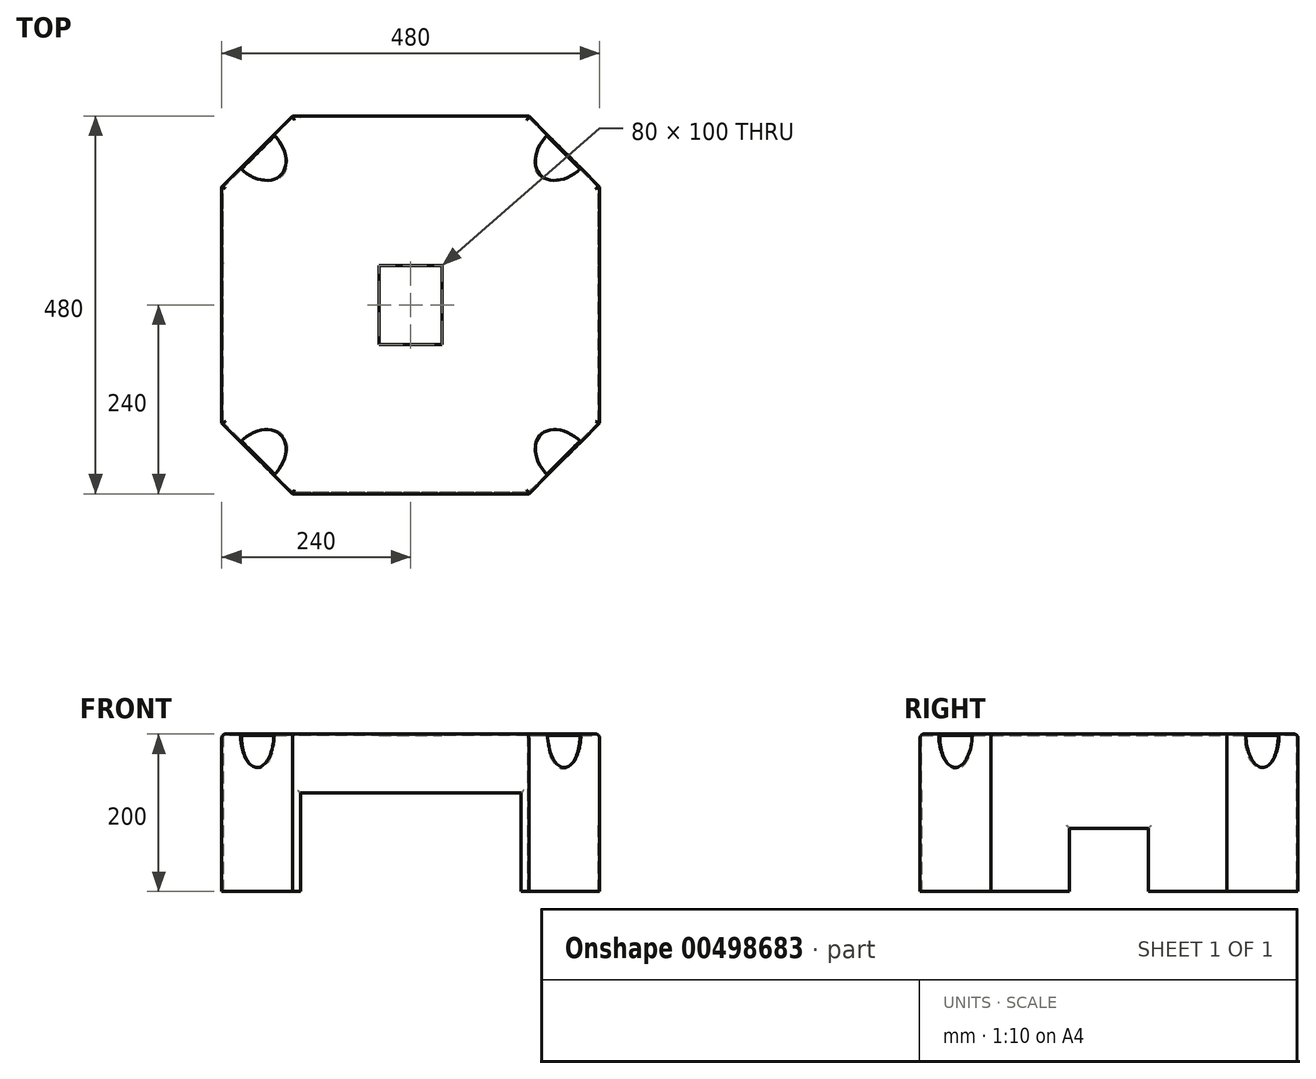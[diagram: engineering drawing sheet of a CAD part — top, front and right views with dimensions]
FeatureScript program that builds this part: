
annotation { "Feature Type Name" : "Feature", "Feature Type Description" : "" }
export const myFeature = defineFeature(function(context is Context, id is Id, definition is map)
    precondition{}
    {
        {
            var Q0;
            Q0=qCreatedBy(makeId("Front.planeOp"),FACE);
            var sketch = newSketch(context, id + "F0", { "sketchPlane" : qUnion([Q0])});
            skLineSegment(sketch, "E0.bottom", {"start": v(240, -100) * mm, "end": v(-240, -100) * mm});
            skLineSegment(sketch, "E0.top", {"start": v(240, 100) * mm, "end": v(-240, 100) * mm});
            skLineSegment(sketch, "E0.left", {"start": v(240, -100) * mm, "end": v(240, 100) * mm});
            skLineSegment(sketch, "E0.right", {"start": v(-240, -100) * mm, "end": v(-240, 100) * mm});
            skPoint(sketch, "E0.middle", {"position": v(0, 0) * mm});
            skLineSegment(sketch, "E1", {"start": v(0, 0) * mm, "end": v(0, -124.49) * mm, "construction": true});
            skPoint(sketch, "E1.endSnap0", {"position": v(0, -100) * mm});
            skLineSegment(sketch, "E2", {"start": v(0, -100) * mm, "end": v(140, -100) * mm});
            skLineSegment(sketch, "E3", {"start": v(140, -100) * mm, "end": v(140, 25) * mm});
            skLineSegment(sketch, "E4", {"start": v(140, 25) * mm, "end": v(-140, 25) * mm});
            skLineSegment(sketch, "E5", {"start": v(-140, 25) * mm, "end": v(-140, -100) * mm});
            skLineSegment(sketch, "E6", {"start": v(-140, -100) * mm, "end": v(0, -100) * mm});
            skSolve(sketch);
        }
        {
            var Q0;
            Q0=makeQuery(id+"F0.imprint","IMPRINT",FACE,{"disambiguationData":[TD([[makeQuery(id+"F0.imprint","IMPRINT",EDGE,{"derivedFrom":sQuery(id+"F0.wireOp",EDGE,"E0.top")}),1.0]])]});
            extrude(context, id + "F1", {"entities" : qUnion([Q0]), "endBound" : BoundingType.SYMMETRIC, "depth" : 480 * mm});
        }
        {
            var Q0;
            Q0=makeQuery(id+"F1.opExtrude","CAP_EDGE",EDGE,{"disambiguationData":[OSD([sQuery(id+"F0.wireOp",EDGE,"E0.left")])],"isStart":false});
            var Q1;
            Q1=makeQuery(id+"F1.opExtrude","CAP_EDGE",EDGE,{"disambiguationData":[OSD([sQuery(id+"F0.wireOp",EDGE,"E0.left")])],"isStart":true});
            var Q2;
            Q2=makeQuery(id+"F1.opExtrude","CAP_EDGE",EDGE,{"disambiguationData":[OSD([sQuery(id+"F0.wireOp",EDGE,"E0.right")])],"isStart":true});
            var Q3;
            Q3=makeQuery(id+"F1.opExtrude","CAP_EDGE",EDGE,{"disambiguationData":[OSD([sQuery(id+"F0.wireOp",EDGE,"E0.right")])],"isStart":false});
            chamfer(context, id + "F2", {"entities" : qUnion([Q0, Q1, Q2, Q3]), "width" : 90 * mm, "tangentPropagation" : true});
        }
        {
            var Q0;
            {var subQ0=sQuery(id+"F0.wireOp",EDGE,"E0.bottom");Q0=makeQuery(id+"F1.opExtrude","SWEPT_FACE",FACE,{"disambiguationData":[OSD([subQ0]),TDD([makeQuery(id+"F0.imprint","IMPRINT",EDGE,{"disambiguationData":[TD([[makeQuery(id+"F0.imprint","INTERSECT",VERTEX,{"derivedFrom":[subQ0,sQuery(id+"F0.wireOp",EDGE,"E0.left")]}),-1.0]])],"derivedFrom":subQ0})])]});}
            var Q1;
            {var subQ0=sQuery(id+"F0.wireOp",EDGE,"E0.bottom");Q1=makeQuery(id+"F1.opExtrude","SWEPT_FACE",FACE,{"disambiguationData":[OSD([subQ0]),TDD([makeQuery(id+"F0.imprint","IMPRINT",EDGE,{"disambiguationData":[TD([[makeQuery(id+"F0.imprint","INTERSECT",VERTEX,{"derivedFrom":[subQ0,sQuery(id+"F0.wireOp",EDGE,"E0.right")]}),1.0]])],"derivedFrom":subQ0})])]});}
            var Q2;
            Q2=makeQuery(id+"F1.opExtrude","SWEPT_FACE",FACE,{"disambiguationData":[OSD([sQuery(id+"F0.wireOp",EDGE,"E4")])]});
            var Q3;
            Q3=makeQuery(id+"F1.opExtrude","SWEPT_FACE",FACE,{"disambiguationData":[OSD([sQuery(id+"F0.wireOp",EDGE,"E3")])]});
            var Q4;
            Q4=makeQuery(id+"F1.opExtrude","SWEPT_FACE",FACE,{"disambiguationData":[OSD([sQuery(id+"F0.wireOp",EDGE,"E5")])]});
            shell(context, id + "F3", {"entities" : qUnion([Q0, Q1, Q2, Q3, Q4]), "thickness" : 1.6 * mm});
        }
        {
            var Q0;
            Q0=makeQuery(id+"F2.opChamfer","BLEND_EDGE",EDGE,{"blendedFrom":[makeQuery(id+"F1.opExtrude","CAP_EDGE",EDGE,{"disambiguationData":[OSD([sQuery(id+"F0.wireOp",EDGE,"E0.right")])],"isStart":true}),makeQuery(id+"F1.opExtrude","SWEPT_FACE",FACE,{"disambiguationData":[OSD([sQuery(id+"F0.wireOp",EDGE,"E0.top")])]})],"blendedInto":[makeQuery(id+"F1.opExtrude","SWEPT_FACE",FACE,{"disambiguationData":[OSD([sQuery(id+"F0.wireOp",EDGE,"E0.top")])]})]});
            cPlane(context, id + "F4", {"entities" : qUnion([Q0]), "cplaneType" : CPlaneType.LINE_ANGLE, "offset" : 25 * mm, "angle" : 45 * degree, "width" : 150 * mm, "height" : 150 * mm});
        }
        {
            var Q0;
            Q0=makeQuery(id+"F2.opChamfer","BLEND_EDGE",EDGE,{"blendedFrom":[makeQuery(id+"F1.opExtrude","CAP_EDGE",EDGE,{"disambiguationData":[OSD([sQuery(id+"F0.wireOp",EDGE,"E0.right")])],"isStart":false}),makeQuery(id+"F1.opExtrude","SWEPT_FACE",FACE,{"disambiguationData":[OSD([sQuery(id+"F0.wireOp",EDGE,"E0.top")])]})],"blendedInto":[makeQuery(id+"F1.opExtrude","SWEPT_FACE",FACE,{"disambiguationData":[OSD([sQuery(id+"F0.wireOp",EDGE,"E0.top")])]})]});
            cPlane(context, id + "F5", {"entities" : qUnion([Q0]), "cplaneType" : CPlaneType.LINE_ANGLE, "offset" : 25 * mm, "angle" : 45 * degree, "oppositeDirection" : true, "width" : 150 * mm, "height" : 150 * mm});
        }
        {
            var Q0;
            Q0=makeQuery(id+"F2.opChamfer","BLEND_EDGE",EDGE,{"blendedFrom":[makeQuery(id+"F1.opExtrude","CAP_EDGE",EDGE,{"disambiguationData":[OSD([sQuery(id+"F0.wireOp",EDGE,"E0.left")])],"isStart":false}),makeQuery(id+"F1.opExtrude","SWEPT_FACE",FACE,{"disambiguationData":[OSD([sQuery(id+"F0.wireOp",EDGE,"E0.top")])]})],"blendedInto":[makeQuery(id+"F1.opExtrude","SWEPT_FACE",FACE,{"disambiguationData":[OSD([sQuery(id+"F0.wireOp",EDGE,"E0.top")])]})]});
            cPlane(context, id + "F6", {"entities" : qUnion([Q0]), "cplaneType" : CPlaneType.LINE_ANGLE, "offset" : 25 * mm, "angle" : 45 * degree, "width" : 150 * mm, "height" : 150 * mm});
        }
        {
            var Q0;
            Q0=makeQuery(id+"F2.opChamfer","BLEND_EDGE",EDGE,{"blendedFrom":[makeQuery(id+"F1.opExtrude","CAP_EDGE",EDGE,{"disambiguationData":[OSD([sQuery(id+"F0.wireOp",EDGE,"E0.left")])],"isStart":true}),makeQuery(id+"F1.opExtrude","SWEPT_FACE",FACE,{"disambiguationData":[OSD([sQuery(id+"F0.wireOp",EDGE,"E0.top")])]})],"blendedInto":[makeQuery(id+"F1.opExtrude","SWEPT_FACE",FACE,{"disambiguationData":[OSD([sQuery(id+"F0.wireOp",EDGE,"E0.top")])]})]});
            cPlane(context, id + "F7", {"entities" : qUnion([Q0]), "cplaneType" : CPlaneType.LINE_ANGLE, "offset" : 25 * mm, "angle" : 45 * degree, "oppositeDirection" : true, "width" : 150 * mm, "height" : 150 * mm});
        }
        {
            var Q0;
            Q0=qCreatedBy(id+"F6.planeOp",FACE);
            var sketch = newSketch(context, id + "F8", { "sketchPlane" : qUnion([Q0])});
            skCircle(sketch, "E7", {"center": v(71.76, -101.48) * mm, "radius": 30 * mm});
            skPoint(sketch, "E8.trimOffspring.end.orphan", {"position": v(123.72, -64.74) * mm});
            skPoint(sketch, "E9.0.start.orphan", {"position": v(19.8, -138.22) * mm});
            skSolve(sketch);
        }
        {
            var Q0;
            Q0=qCreatedBy(id+"F7.planeOp",FACE);
            var sketch = newSketch(context, id + "F9", { "sketchPlane" : qUnion([Q0])});
            skCircle(sketch, "E10", {"center": v(71.76, -101.48) * mm, "radius": 30 * mm});
            skPoint(sketch, "E11.trimOffspring.end.orphan", {"position": v(19.8, -138.22) * mm});
            skPoint(sketch, "E12.0.start.orphan", {"position": v(123.72, -64.74) * mm});
            skSolve(sketch);
        }
        {
            var Q0;
            Q0=qCreatedBy(id+"F4.planeOp",FACE);
            var sketch = newSketch(context, id + "F10", { "sketchPlane" : qUnion([Q0])});
            skCircle(sketch, "E13", {"center": v(-71.76, -101.48) * mm, "radius": 30 * mm});
            skPoint(sketch, "E14.orphan", {"position": v(-19.8, -138.22) * mm});
            skPoint(sketch, "E15.0.end.orphan", {"position": v(-123.72, -64.74) * mm});
            skSolve(sketch);
        }
        {
            var Q0;
            Q0=qCreatedBy(id+"F5.planeOp",FACE);
            var sketch = newSketch(context, id + "F11", { "sketchPlane" : qUnion([Q0])});
            skCircle(sketch, "E16", {"center": v(-71.76, -101.48) * mm, "radius": 30 * mm});
            skPoint(sketch, "E17.orphan", {"position": v(-123.72, -64.74) * mm});
            skPoint(sketch, "E18.0.end.orphan", {"position": v(-19.8, -138.22) * mm});
            skSolve(sketch);
        }
        {
            var Q0;
            Q0=makeQuery(id+"F10.imprint","IMPRINT",FACE,{"disambiguationData":[TD([[makeQuery(id+"F10.imprint","IMPRINT",EDGE,{"derivedFrom":sQuery(id+"F10.wireOp",EDGE,"E13")}),1.0]])]});
            extrude(context, id + "F12", {"entities" : qUnion([Q0]), "operationType" : NewBodyOperationType.REMOVE, "depth" : 78 * mm});
        }
        {
            var Q0;
            Q0=makeQuery(id+"F11.imprint","IMPRINT",FACE,{"disambiguationData":[TD([[makeQuery(id+"F11.imprint","IMPRINT",EDGE,{"derivedFrom":sQuery(id+"F11.wireOp",EDGE,"E16")}),1.0]])]});
            extrude(context, id + "F13", {"entities" : qUnion([Q0]), "operationType" : NewBodyOperationType.REMOVE, "oppositeDirection" : true, "depth" : 82 * mm});
        }
        {
            var Q0;
            Q0=makeQuery(id+"F8.imprint","IMPRINT",FACE,{"disambiguationData":[TD([[makeQuery(id+"F8.imprint","IMPRINT",EDGE,{"derivedFrom":sQuery(id+"F8.wireOp",EDGE,"E7")}),1.0]])]});
            extrude(context, id + "F14", {"entities" : qUnion([Q0]), "operationType" : NewBodyOperationType.REMOVE, "oppositeDirection" : true, "depth" : 153 * mm});
        }
        {
            var Q0;
            Q0=makeQuery(id+"F9.imprint","IMPRINT",FACE,{"disambiguationData":[TD([[makeQuery(id+"F9.imprint","IMPRINT",EDGE,{"derivedFrom":sQuery(id+"F9.wireOp",EDGE,"E10")}),1.0]])]});
            extrude(context, id + "F15", {"entities" : qUnion([Q0]), "operationType" : NewBodyOperationType.REMOVE, "depth" : 141 * mm});
        }
        {
            var Q0;
            Q0=makeQuery(id+"F1.opExtrude","SWEPT_FACE",FACE,{"disambiguationData":[OSD([sQuery(id+"F0.wireOp",EDGE,"E0.right")])]});
            var sketch = newSketch(context, id + "F16", { "sketchPlane" : qUnion([Q0])});
            skLineSegment(sketch, "E19.0.0", {"start": v(-50, -100) * mm, "end": v(50, -100) * mm});
            skPoint(sketch, "E20.endSnap0", {"position": v(0, -100) * mm});
            skLineSegment(sketch, "E21", {"start": v(0, -100) * mm, "end": v(-50, -100) * mm});
            skLineSegment(sketch, "E22", {"start": v(-50, -100) * mm, "end": v(-50, -20) * mm});
            skLineSegment(sketch, "E23", {"start": v(-50, -20) * mm, "end": v(50, -20) * mm});
            skLineSegment(sketch, "E24", {"start": v(50, -20) * mm, "end": v(50, -100) * mm});
            skLineSegment(sketch, "E25", {"start": v(50, -100) * mm, "end": v(0, -100) * mm});
            skPoint(sketch, "E19.0.1.start.orphan", {"position": v(150, -100) * mm});
            skPoint(sketch, "E19.0.2.start.orphan", {"position": v(150, 100) * mm});
            skPoint(sketch, "E19.0.3.end.orphan", {"position": v(-150, -100) * mm});
            skPoint(sketch, "E19.0.3.start.orphan", {"position": v(-150, 100) * mm});
            skPoint(sketch, "E20.end.orphan", {"position": v(0, -20) * mm});
            skSolve(sketch);
        }
        {
            var Q0;
            Q0 = qSketchRegion(id + "F16", true);
            extrude(context, id + "F17", {"entities" : qUnion([Q0]), "operationType" : NewBodyOperationType.REMOVE, "oppositeDirection" : true, "depth" : 688 * mm});
        }
        {
            var Q0;
            Q0=makeQuery(id+"F1.opExtrude","SWEPT_FACE",FACE,{"disambiguationData":[OSD([sQuery(id+"F0.wireOp",EDGE,"E0.top")])]});
            var sketch = newSketch(context, id + "F18", { "sketchPlane" : qUnion([Q0])});
            skLineSegment(sketch, "E26.bottom", {"start": v(40, -50) * mm, "end": v(-40, -50) * mm});
            skLineSegment(sketch, "E26.top", {"start": v(40, 50) * mm, "end": v(-40, 50) * mm});
            skLineSegment(sketch, "E26.left", {"start": v(40, -50) * mm, "end": v(40, 50) * mm});
            skLineSegment(sketch, "E26.right", {"start": v(-40, -50) * mm, "end": v(-40, 50) * mm});
            skPoint(sketch, "E26.middle", {"position": v(0, 0) * mm});
            skPoint(sketch, "E27.0.3.start.orphan", {"position": v(-150, 240) * mm});
            skPoint(sketch, "E27.0.4.end.orphan", {"position": v(-173.79, 216.21) * mm});
            skPoint(sketch, "E27.0.5.start.orphan", {"position": v(-216.21, 173.79) * mm});
            skPoint(sketch, "E27.0.6.start.orphan", {"position": v(-240, 150) * mm});
            skPoint(sketch, "E27.0.7.start.orphan", {"position": v(-240, -150) * mm});
            skPoint(sketch, "E27.0.8.end.orphan", {"position": v(-216.21, -173.79) * mm});
            skPoint(sketch, "E27.0.9.start.orphan", {"position": v(-173.79, -216.21) * mm});
            skPoint(sketch, "E27.0.10.start.orphan", {"position": v(-150, -240) * mm});
            skPoint(sketch, "E27.0.11.start.orphan", {"position": v(150, -240) * mm});
            skPoint(sketch, "E27.0.12.end.orphan", {"position": v(173.79, -216.21) * mm});
            skPoint(sketch, "E27.0.13.start.orphan", {"position": v(216.21, -173.79) * mm});
            skPoint(sketch, "E27.0.14.start.orphan", {"position": v(240, -150) * mm});
            skPoint(sketch, "E27.0.15.start.orphan", {"position": v(240, 150) * mm});
            skPoint(sketch, "E27.0.1.end.orphan", {"position": v(150, 240) * mm});
            skPoint(sketch, "E27.0.0.end.orphan", {"position": v(216.21, 173.79) * mm});
            skPoint(sketch, "E27.0.0.start.orphan", {"position": v(173.79, 216.21) * mm});
            skLineSegment(sketch, "E28", {"start": v(0, -50) * mm, "end": v(0, 59.6) * mm, "construction": true});
            skSolve(sketch);
        }
        {
            var Q0;
            Q0 = qSketchRegion(id + "F18", true);
            extrude(context, id + "F19", {"entities" : qUnion([Q0]), "operationType" : NewBodyOperationType.REMOVE, "oppositeDirection" : true, "depth" : 25 * mm});
        }
        {
            var Q0;
            Q0=makeQuery(id+"F1.opExtrude","CAP_EDGE",EDGE,{"disambiguationData":[OSD([sQuery(id+"F0.wireOp",EDGE,"E0.top")])],"isStart":true});
            var Q1;
            {var subQ0=sQuery(id+"F0.wireOp",EDGE,"E0.right");var subQ1=sQuery(id+"F0.wireOp",EDGE,"E0.top");var subQ2=makeQuery(id+"F1.opExtrude","SWEPT_FACE",FACE,{"disambiguationData":[OSD([subQ1])]});var subQ3=makeQuery(id+"F1.opExtrude","CAP_EDGE",EDGE,{"disambiguationData":[OSD([subQ0])],"isStart":true});Q1=makeQuery(id+"F12.boolean.opBoolean","SPLIT",EDGE,{"disambiguationData":[TD([makeQuery(id+"F1.opExtrude","CAP_FACE",FACE,{"disambiguationData":[OSD([sQuery(id+"F0.wireOp",EDGE,"E0.bottom"),subQ1,sQuery(id+"F0.wireOp",EDGE,"E0.left"),subQ0,sQuery(id+"F0.wireOp",EDGE,"E3"),sQuery(id+"F0.wireOp",EDGE,"E4"),sQuery(id+"F0.wireOp",EDGE,"E5")])],"isStart":true})])],"derivedFrom":makeQuery(id+"F2.opChamfer","BLEND_EDGE",EDGE,{"blendedFrom":[subQ3,subQ2],"blendedInto":[subQ2]})});}
            var Q2;
            {var subQ0=sQuery(id+"F0.wireOp",EDGE,"E0.left");var subQ1=sQuery(id+"F0.wireOp",EDGE,"E0.top");var subQ2=makeQuery(id+"F1.opExtrude","CAP_EDGE",EDGE,{"disambiguationData":[OSD([subQ0])],"isStart":true});var subQ3=makeQuery(id+"F1.opExtrude","SWEPT_FACE",FACE,{"disambiguationData":[OSD([subQ1])]});Q2=makeQuery(id+"F15.boolean.opBoolean","SPLIT",EDGE,{"disambiguationData":[TD([makeQuery(id+"F1.opExtrude","CAP_FACE",FACE,{"disambiguationData":[OSD([sQuery(id+"F0.wireOp",EDGE,"E0.bottom"),subQ1,subQ0,sQuery(id+"F0.wireOp",EDGE,"E0.right"),sQuery(id+"F0.wireOp",EDGE,"E3"),sQuery(id+"F0.wireOp",EDGE,"E4"),sQuery(id+"F0.wireOp",EDGE,"E5")])],"isStart":true})])],"derivedFrom":makeQuery(id+"F2.opChamfer","BLEND_EDGE",EDGE,{"blendedFrom":[subQ2,subQ3],"blendedInto":[subQ3]})});}
            var Q3;
            {var subQ0=makeQuery(id+"F1.opExtrude","SWEPT_FACE",FACE,{"disambiguationData":[OSD([sQuery(id+"F0.wireOp",EDGE,"E0.top")])]});var subQ1=sQuery(id+"F0.wireOp",EDGE,"E0.left");var subQ2=makeQuery(id+"F1.opExtrude","CAP_EDGE",EDGE,{"disambiguationData":[OSD([subQ1])],"isStart":true});Q3=makeQuery(id+"F15.boolean.opBoolean","SPLIT",EDGE,{"disambiguationData":[TD([makeQuery(id+"F1.opExtrude","SWEPT_FACE",FACE,{"disambiguationData":[OSD([subQ1])]})])],"derivedFrom":makeQuery(id+"F2.opChamfer","BLEND_EDGE",EDGE,{"blendedFrom":[subQ2,subQ0],"blendedInto":[subQ0]})});}
            var Q4;
            {var subQ0=makeQuery(id+"F1.opExtrude","SWEPT_FACE",FACE,{"disambiguationData":[OSD([sQuery(id+"F0.wireOp",EDGE,"E0.top")])]});var subQ1=sQuery(id+"F0.wireOp",EDGE,"E0.right");var subQ2=makeQuery(id+"F1.opExtrude","CAP_EDGE",EDGE,{"disambiguationData":[OSD([subQ1])],"isStart":true});Q4=makeQuery(id+"F12.boolean.opBoolean","SPLIT",EDGE,{"disambiguationData":[TD([makeQuery(id+"F1.opExtrude","SWEPT_FACE",FACE,{"disambiguationData":[OSD([subQ1])]})])],"derivedFrom":makeQuery(id+"F2.opChamfer","BLEND_EDGE",EDGE,{"blendedFrom":[subQ2,subQ0],"blendedInto":[subQ0]})});}
            var Q5;
            Q5=makeQuery(id+"F1.opExtrude","SWEPT_EDGE",EDGE,{"disambiguationData":[OSD([sQuery(id+"F0.wireOp",EDGE,"E0.top"),sQuery(id+"F0.wireOp",EDGE,"E0.right")])]});
            var Q6;
            {var subQ0=makeQuery(id+"F1.opExtrude","SWEPT_FACE",FACE,{"disambiguationData":[OSD([sQuery(id+"F0.wireOp",EDGE,"E0.top")])]});var subQ1=sQuery(id+"F0.wireOp",EDGE,"E0.right");var subQ2=makeQuery(id+"F1.opExtrude","CAP_EDGE",EDGE,{"disambiguationData":[OSD([subQ1])],"isStart":false});Q6=makeQuery(id+"F13.boolean.opBoolean","SPLIT",EDGE,{"disambiguationData":[TD([makeQuery(id+"F1.opExtrude","SWEPT_FACE",FACE,{"disambiguationData":[OSD([subQ1])]})])],"derivedFrom":makeQuery(id+"F2.opChamfer","BLEND_EDGE",EDGE,{"blendedFrom":[subQ2,subQ0],"blendedInto":[subQ0]})});}
            var Q7;
            {var subQ0=sQuery(id+"F0.wireOp",EDGE,"E0.right");var subQ1=sQuery(id+"F0.wireOp",EDGE,"E0.top");var subQ2=makeQuery(id+"F1.opExtrude","SWEPT_FACE",FACE,{"disambiguationData":[OSD([subQ1])]});var subQ3=makeQuery(id+"F1.opExtrude","CAP_EDGE",EDGE,{"disambiguationData":[OSD([subQ0])],"isStart":false});Q7=makeQuery(id+"F13.boolean.opBoolean","SPLIT",EDGE,{"disambiguationData":[TD([makeQuery(id+"F1.opExtrude","CAP_FACE",FACE,{"disambiguationData":[OSD([sQuery(id+"F0.wireOp",EDGE,"E0.bottom"),subQ1,sQuery(id+"F0.wireOp",EDGE,"E0.left"),subQ0,sQuery(id+"F0.wireOp",EDGE,"E3"),sQuery(id+"F0.wireOp",EDGE,"E4"),sQuery(id+"F0.wireOp",EDGE,"E5")])],"isStart":false})])],"derivedFrom":makeQuery(id+"F2.opChamfer","BLEND_EDGE",EDGE,{"blendedFrom":[subQ3,subQ2],"blendedInto":[subQ2]})});}
            var Q8;
            Q8=makeQuery(id+"F1.opExtrude","CAP_EDGE",EDGE,{"disambiguationData":[OSD([sQuery(id+"F0.wireOp",EDGE,"E0.top")])],"isStart":false});
            var Q9;
            {var subQ0=makeQuery(id+"F1.opExtrude","SWEPT_FACE",FACE,{"disambiguationData":[OSD([sQuery(id+"F0.wireOp",EDGE,"E0.top")])]});var subQ1=sQuery(id+"F0.wireOp",EDGE,"E0.left");var subQ2=makeQuery(id+"F1.opExtrude","CAP_EDGE",EDGE,{"disambiguationData":[OSD([subQ1])],"isStart":false});Q9=makeQuery(id+"F14.boolean.opBoolean","SPLIT",EDGE,{"disambiguationData":[TD([makeQuery(id+"F1.opExtrude","SWEPT_FACE",FACE,{"disambiguationData":[OSD([subQ1])]})])],"derivedFrom":makeQuery(id+"F2.opChamfer","BLEND_EDGE",EDGE,{"blendedFrom":[subQ2,subQ0],"blendedInto":[subQ0]})});}
            var Q10;
            {var subQ0=sQuery(id+"F0.wireOp",EDGE,"E0.left");var subQ1=sQuery(id+"F0.wireOp",EDGE,"E0.top");var subQ2=makeQuery(id+"F1.opExtrude","CAP_EDGE",EDGE,{"disambiguationData":[OSD([subQ0])],"isStart":false});var subQ3=makeQuery(id+"F1.opExtrude","SWEPT_FACE",FACE,{"disambiguationData":[OSD([subQ1])]});Q10=makeQuery(id+"F14.boolean.opBoolean","SPLIT",EDGE,{"disambiguationData":[TD([makeQuery(id+"F1.opExtrude","CAP_FACE",FACE,{"disambiguationData":[OSD([sQuery(id+"F0.wireOp",EDGE,"E0.bottom"),subQ1,subQ0,sQuery(id+"F0.wireOp",EDGE,"E0.right"),sQuery(id+"F0.wireOp",EDGE,"E3"),sQuery(id+"F0.wireOp",EDGE,"E4"),sQuery(id+"F0.wireOp",EDGE,"E5")])],"isStart":false})])],"derivedFrom":makeQuery(id+"F2.opChamfer","BLEND_EDGE",EDGE,{"blendedFrom":[subQ2,subQ3],"blendedInto":[subQ3]})});}
            var Q11;
            Q11=makeQuery(id+"F1.opExtrude","SWEPT_EDGE",EDGE,{"disambiguationData":[OSD([sQuery(id+"F0.wireOp",EDGE,"E0.top"),sQuery(id+"F0.wireOp",EDGE,"E0.left")])]});
            var Q12;
            {var subQ0=sQuery(id+"F0.wireOp",EDGE,"E3");Q12=makeQuery(id+"F3.opShell","OFFSET_EDGE",EDGE,{"disambiguationData":[OSD([subQ0]),TDD([makeQuery(id+"F1.opExtrude","CAP_EDGE",EDGE,{"disambiguationData":[OSD([subQ0])],"isStart":false})])]});}
            var Q13;
            {var subQ0=sQuery(id+"F0.wireOp",EDGE,"E4");Q13=makeQuery(id+"F3.opShell","OFFSET_EDGE",EDGE,{"disambiguationData":[OSD([subQ0]),TDD([makeQuery(id+"F1.opExtrude","CAP_EDGE",EDGE,{"disambiguationData":[OSD([subQ0])],"isStart":false})])]});}
            var Q14;
            {var subQ0=sQuery(id+"F0.wireOp",EDGE,"E5");Q14=makeQuery(id+"F3.opShell","OFFSET_EDGE",EDGE,{"disambiguationData":[OSD([subQ0]),TDD([makeQuery(id+"F1.opExtrude","CAP_EDGE",EDGE,{"disambiguationData":[OSD([subQ0])],"isStart":false})])]});}
            var Q15;
            {var subQ0=sQuery(id+"F0.wireOp",EDGE,"E0.right");Q15=makeQuery(id+"F17.boolean.opBoolean","INTERSECT",EDGE,{"derivedFrom":[makeQuery(id+"F3.opShell","OFFSET_FACE",FACE,{"disambiguationData":[OSD([subQ0]),TDD([makeQuery(id+"F1.opExtrude","SWEPT_FACE",FACE,{"disambiguationData":[OSD([subQ0])]})])]}),makeQuery(id+"F17.opExtrude","SWEPT_FACE",FACE,{"disambiguationData":[OSD([sQuery(id+"F16.wireOp",EDGE,"E24")])]})]});}
            var Q16;
            {var subQ0=sQuery(id+"F0.wireOp",EDGE,"E0.right");Q16=makeQuery(id+"F17.boolean.opBoolean","INTERSECT",EDGE,{"derivedFrom":[makeQuery(id+"F3.opShell","OFFSET_FACE",FACE,{"disambiguationData":[OSD([subQ0]),TDD([makeQuery(id+"F1.opExtrude","SWEPT_FACE",FACE,{"disambiguationData":[OSD([subQ0])]})])]}),makeQuery(id+"F17.opExtrude","SWEPT_FACE",FACE,{"disambiguationData":[OSD([sQuery(id+"F16.wireOp",EDGE,"E22")])]})]});}
            var Q17;
            {var subQ0=sQuery(id+"F0.wireOp",EDGE,"E0.right");Q17=makeQuery(id+"F17.boolean.opBoolean","INTERSECT",EDGE,{"derivedFrom":[makeQuery(id+"F3.opShell","OFFSET_FACE",FACE,{"disambiguationData":[OSD([subQ0]),TDD([makeQuery(id+"F1.opExtrude","SWEPT_FACE",FACE,{"disambiguationData":[OSD([subQ0])]})])]}),makeQuery(id+"F17.opExtrude","SWEPT_FACE",FACE,{"disambiguationData":[OSD([sQuery(id+"F16.wireOp",EDGE,"E23")])]})]});}
            var Q18;
            {var subQ0=sQuery(id+"F0.wireOp",EDGE,"E0.left");Q18=makeQuery(id+"F17.boolean.opBoolean","INTERSECT",EDGE,{"derivedFrom":[makeQuery(id+"F3.opShell","OFFSET_FACE",FACE,{"disambiguationData":[OSD([subQ0]),TDD([makeQuery(id+"F1.opExtrude","SWEPT_FACE",FACE,{"disambiguationData":[OSD([subQ0])]})])]}),makeQuery(id+"F17.opExtrude","SWEPT_FACE",FACE,{"disambiguationData":[OSD([sQuery(id+"F16.wireOp",EDGE,"E24")])]})]});}
            var Q19;
            {var subQ0=sQuery(id+"F0.wireOp",EDGE,"E0.left");Q19=makeQuery(id+"F17.boolean.opBoolean","INTERSECT",EDGE,{"derivedFrom":[makeQuery(id+"F3.opShell","OFFSET_FACE",FACE,{"disambiguationData":[OSD([subQ0]),TDD([makeQuery(id+"F1.opExtrude","SWEPT_FACE",FACE,{"disambiguationData":[OSD([subQ0])]})])]}),makeQuery(id+"F17.opExtrude","SWEPT_FACE",FACE,{"disambiguationData":[OSD([sQuery(id+"F16.wireOp",EDGE,"E23")])]})]});}
            var Q20;
            {var subQ0=sQuery(id+"F0.wireOp",EDGE,"E0.left");Q20=makeQuery(id+"F17.boolean.opBoolean","INTERSECT",EDGE,{"derivedFrom":[makeQuery(id+"F3.opShell","OFFSET_FACE",FACE,{"disambiguationData":[OSD([subQ0]),TDD([makeQuery(id+"F1.opExtrude","SWEPT_FACE",FACE,{"disambiguationData":[OSD([subQ0])]})])]}),makeQuery(id+"F17.opExtrude","SWEPT_FACE",FACE,{"disambiguationData":[OSD([sQuery(id+"F16.wireOp",EDGE,"E22")])]})]});}
            var Q21;
            Q21=makeQuery(id+"F1.opExtrude","CAP_EDGE",EDGE,{"disambiguationData":[OSD([sQuery(id+"F0.wireOp",EDGE,"E4")])],"isStart":true});
            var Q22;
            Q22=makeQuery(id+"F1.opExtrude","CAP_EDGE",EDGE,{"disambiguationData":[OSD([sQuery(id+"F0.wireOp",EDGE,"E3")])],"isStart":true});
            var Q23;
            Q23=makeQuery(id+"F1.opExtrude","CAP_EDGE",EDGE,{"disambiguationData":[OSD([sQuery(id+"F0.wireOp",EDGE,"E5")])],"isStart":true});
            fillet(context, id + "F20", {"entities" : qUnion([Q0, Q1, Q2, Q3, Q4, Q5, Q6, Q7, Q8, Q9, Q10, Q11, Q12, Q13, Q14, Q15, Q16, Q17, Q18, Q19, Q20, Q21, Q22, Q23]), "radius" : 5 * mm, "tangentPropagation" : true, "allowEdgeOverflow" : false});
        }
    });
